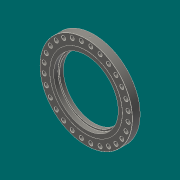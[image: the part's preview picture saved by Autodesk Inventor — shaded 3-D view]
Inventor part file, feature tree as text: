
AUTODESK INVENTOR PART (.ipt)
format: ipt  version: 2017.3 (Build 213257000, 257)  size: 306,176 bytes
history: native  units: in
note: dims shown in document units (in); Inventor stores cm internally (conversion verified against a paired STEP export)
features: sketch x6, extrude x4, chamfer x3, hole x2, pattern_circular x2, fillet x1, plane x1, projected_geometry x1
ambient origin geometry x8: Origin, YZ Plane, XZ Plane, XY Plane, X Axis, Y Axis, Z Axis, Center Point
bodies: Solid1 (feature_tree)
feature tree (20):
  extrude  "Extrusion: OD"  Depth=3.6777in TaperAngle=0.0deg
  extrude  "Extrusion: RF"  Depth=0.0625in TaperAngle=0.0deg
  extrude  "Extrusion: ID Large"  Depth=2.0in TaperAngle=0.0deg
  extrude  "Extrusion: ID Small"  Depth=39.25in
  hole  "Hole: Bolt"  [1 undecoded]
  chamfer  "Chamfer: Bolt hole"  Distance=0.0625in Angle=45.0deg
  pattern_circular  "Circular Pattern: Bolt hole"  Angle=45.0deg  [1 undecoded]
  chamfer  "Chamfer: OD"  Distance=0.0312in
  chamfer  "Chamfer2"  [1 undecoded]
  fillet  "Fillet2"  Radius=0.0625in
  plane  "Work Plane1"
  hole  "Hole2"  [1 undecoded]
  pattern_circular  "Circular Pattern2"  Count=2 Angle=360.0deg
  sketch  "Sketch1"  dims[d0=43.0in d1=3.6777in d2=0.0in]
  sketch  "Sketch2"  dims[d3=33.75in d4=0.0625in d5=0.0in]
  sketch  "Sketch3"  dims[d6=30.0in d7=2.0in d8=0.0in]
  sketch  "Sketch4"  dims[d10=2.0in d11=0.0in d12=39.25in]
  sketch  "Sketch5"  dims[d13=0.0442in]
  sketch  "Sketch6"  dims[d14=1.875in d15=0.75in d16=0.375in d17=0.25in d18=0.5635in d19=1.0in d20=0.8108in d21=11.0236in d22=360.0deg d24=0.0625in d25=0.125in d26=45.0deg d28=0.0312in d29=0.125in d30=45.0deg d31=0.0312in d32=0.0in d33=0.0625in d34=0.125in d35=45.0deg d36=1.8701in d37=0.642in d38=2.0in d39=0.375in d40=0.25in d41=0.5635in d42=2.5in d43=0.8108in d44=0.7874in d45=360.0deg]
  projected_geometry  "Projected Loop1"
note: 4 required parameter values undecoded (feature->parameter linkage not recoverable at this tier; creation-order binding heuristic only, values carry confidence <= 0.55)
